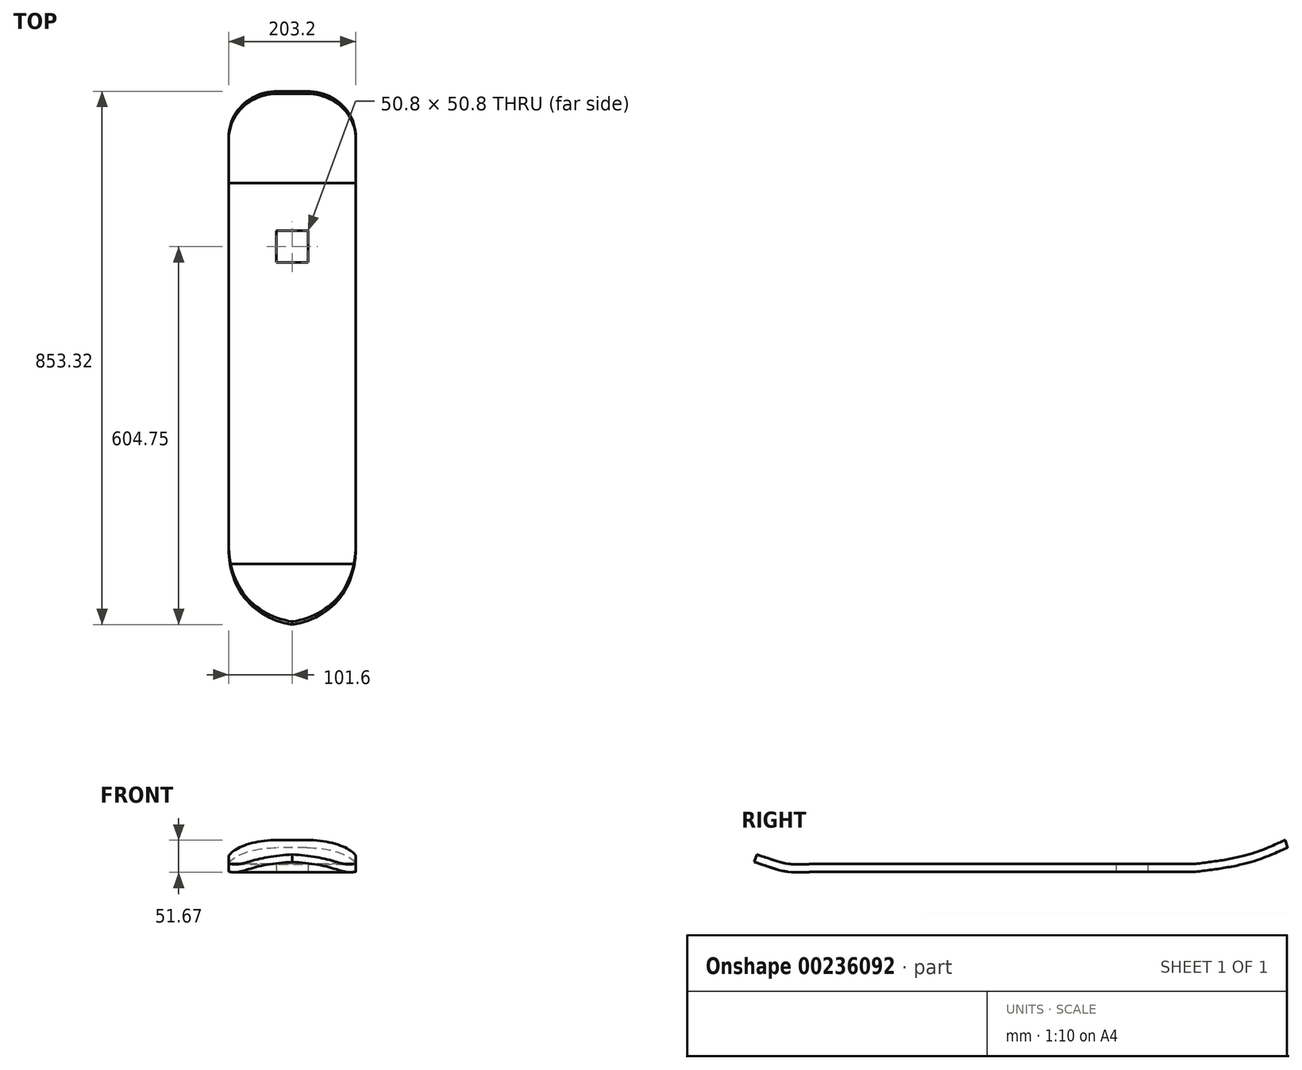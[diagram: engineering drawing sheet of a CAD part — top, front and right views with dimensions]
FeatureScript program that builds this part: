
annotation { "Feature Type Name" : "Feature", "Feature Type Description" : "" }
export const myFeature = defineFeature(function(context is Context, id is Id, definition is map)
    precondition{}
    {
        {
            var Q0;
            Q0=qCreatedBy(makeId("Top.planeOp"),FACE);
            var sketch = newSketch(context, id + "F0", { "sketchPlane" : qUnion([Q0])});
            skLineSegment(sketch, "E0.bottom", {"start": v(101.6, 304.8) * mm, "end": v(-101.6, 304.8) * mm});
            skLineSegment(sketch, "E0.top", {"start": v(101.6, -304.8) * mm, "end": v(-101.6, -304.8) * mm});
            skLineSegment(sketch, "E0.left", {"start": v(101.6, 304.8) * mm, "end": v(101.6, -304.8) * mm});
            skLineSegment(sketch, "E0.right", {"start": v(-101.6, 304.8) * mm, "end": v(-101.6, -304.8) * mm});
            skPoint(sketch, "E0.middle", {"position": v(0, 0) * mm});
            skLineSegment(sketch, "E1.bottom", {"start": v(25.4, 177.8) * mm, "end": v(-25.4, 177.8) * mm});
            skLineSegment(sketch, "E1.top", {"start": v(25.4, 228.6) * mm, "end": v(-25.4, 228.6) * mm});
            skLineSegment(sketch, "E1.left", {"start": v(25.4, 177.8) * mm, "end": v(25.4, 228.6) * mm});
            skLineSegment(sketch, "E1.right", {"start": v(-25.4, 177.8) * mm, "end": v(-25.4, 228.6) * mm});
            skPoint(sketch, "E1.middle", {"position": v(0, 203.2) * mm});
            skSolve(sketch);
        }
        {
            var Q0;
            Q0 = qSketchRegion(id + "F0", true);
            extrude(context, id + "F1", {"entities" : qUnion([Q0]), "endBound" : BoundingType.SYMMETRIC, "depth" : 12.7 * mm});
        }
        {
            var Q0;
            Q0=qCreatedBy(makeId("Right.planeOp"),FACE);
            var sketch = newSketch(context, id + "F2", { "sketchPlane" : qUnion([Q0])});
            skFitSpline(sketch, "E2", {"points": [v(304.63, 0) * mm, v(357.38, 7.4) * mm, v(405.98, 19.85) * mm, v(449.83, 38.23) * mm], "startDerivative": vector(155.15, 18.65) * mm, "endDerivative": vector(133.02, 60.74) * mm});
            skFitSpline(sketch, "E3", {"points": [v(-305.33, 0) * mm, v(-347.26, 0) * mm, v(-378.9, 8.46) * mm, v(-400.97, 15.82) * mm], "startDerivative": vector(-113.55, -7.07) * mm, "endDerivative": vector(-74.85, 24.72) * mm});
            skSolve(sketch);
        }
        {
            var Q0;
            Q0=makeQuery(id+"F1.opExtrude","SWEPT_FACE",FACE,{"disambiguationData":[OSD([sQuery(id+"F0.wireOp",EDGE,"E0.bottom")])]});
            var Q1;
            Q1=sQuery(id+"F2.wireOp",EDGE,"E2");
            sweep(context, id + "F3", {"operationType" : NewBodyOperationType.ADD, "profiles" : qUnion([Q0]), "path" : qUnion([Q1])});
        }
        {
            var Q0;
            Q0=makeQuery(id+"F1.opExtrude","SWEPT_FACE",FACE,{"disambiguationData":[OSD([sQuery(id+"F0.wireOp",EDGE,"E0.top")])]});
            var Q1;
            Q1=sQuery(id+"F2.wireOp",EDGE,"E3");
            sweep(context, id + "F4", {"operationType" : NewBodyOperationType.ADD, "profiles" : qUnion([Q0]), "path" : qUnion([Q1])});
        }
        {
            var Q0;
            Q0=makeQuery(id+"F4.opSweep","CAP_EDGE",EDGE,{"disambiguationData":[OSD([sQuery(id+"F0.wireOp",EDGE,"E0.top"),sQuery(id+"F0.wireOp",EDGE,"E0.left"),sQuery(id+"F2.wireOp",VERTEX,"E3.end")])],"isStart":false});
            var Q1;
            Q1=makeQuery(id+"F4.opSweep","CAP_EDGE",EDGE,{"disambiguationData":[OSD([sQuery(id+"F0.wireOp",EDGE,"E0.top"),sQuery(id+"F0.wireOp",EDGE,"E0.right"),sQuery(id+"F2.wireOp",VERTEX,"E3.end")])],"isStart":false});
            fillet(context, id + "F5", {"entities" : qUnion([Q0, Q1]), "radius" : 119.58 * mm, "tangentPropagation" : true, "allowEdgeOverflow" : false});
        }
        {
            var Q0;
            Q0=makeQuery(id+"F3.opSweep","CAP_EDGE",EDGE,{"disambiguationData":[OSD([sQuery(id+"F0.wireOp",EDGE,"E0.bottom"),sQuery(id+"F0.wireOp",EDGE,"E0.left"),sQuery(id+"F2.wireOp",VERTEX,"E2.end")])],"isStart":false});
            var Q1;
            Q1=makeQuery(id+"F3.opSweep","CAP_EDGE",EDGE,{"disambiguationData":[OSD([sQuery(id+"F0.wireOp",EDGE,"E0.bottom"),sQuery(id+"F0.wireOp",EDGE,"E0.right"),sQuery(id+"F2.wireOp",VERTEX,"E2.end")])],"isStart":false});
            fillet(context, id + "F6", {"entities" : qUnion([Q0, Q1]), "radius" : 77.88 * mm, "tangentPropagation" : true, "allowEdgeOverflow" : false});
        }
    });
